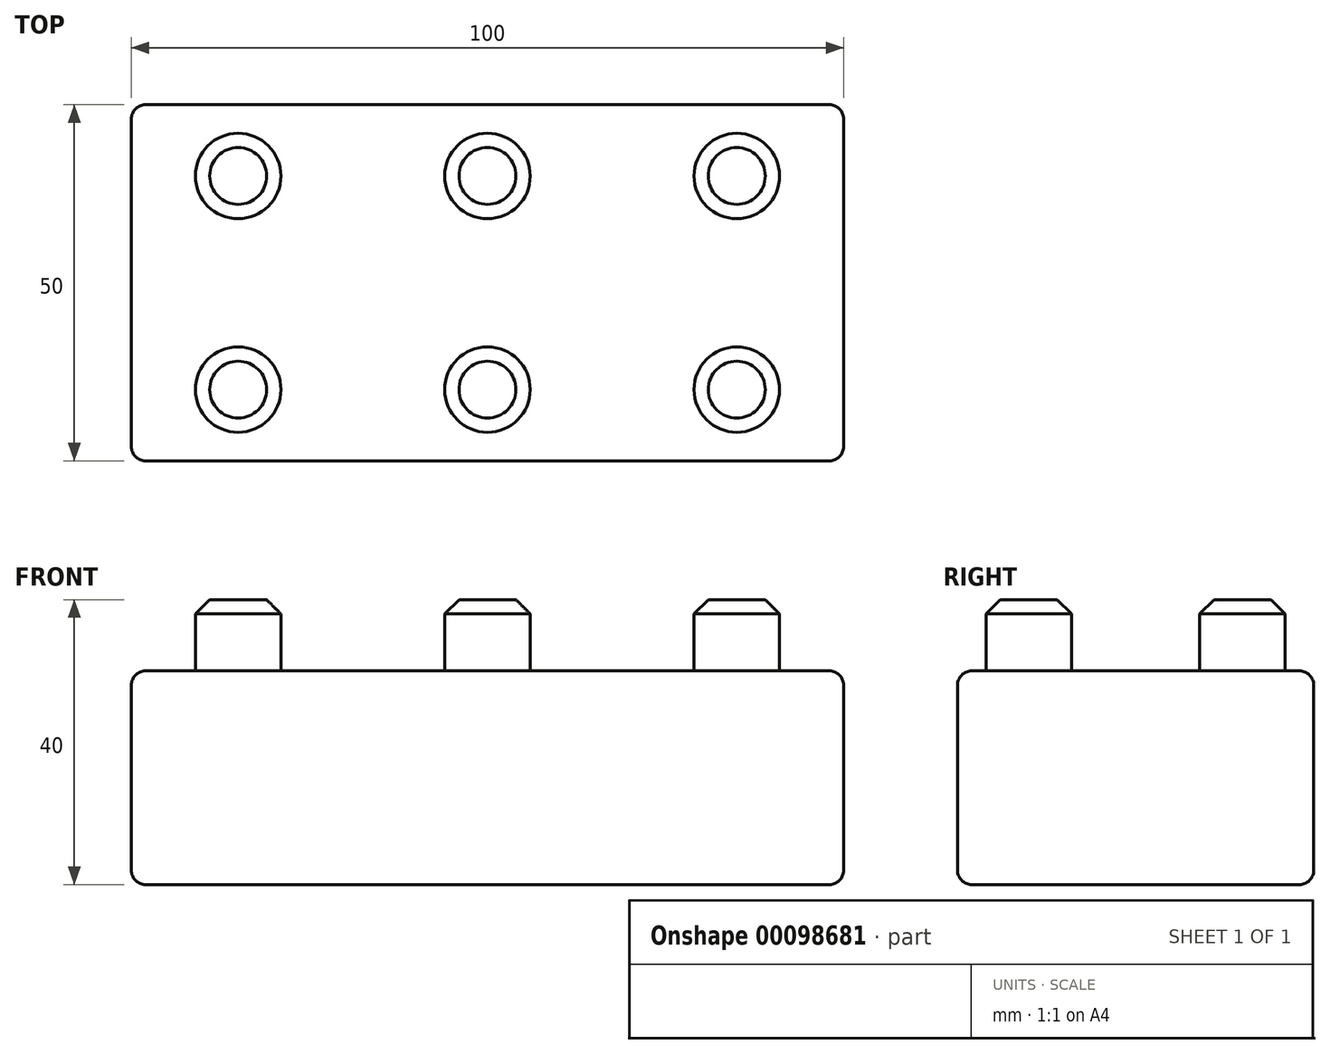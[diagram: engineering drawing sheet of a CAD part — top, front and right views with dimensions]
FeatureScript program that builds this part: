
annotation { "Feature Type Name" : "Feature", "Feature Type Description" : "" }
export const myFeature = defineFeature(function(context is Context, id is Id, definition is map)
    precondition{}
    {
        {
            var Q0;
            Q0=qCreatedBy(makeId("Top.planeOp"),FACE);
            var sketch = newSketch(context, id + "F0", { "sketchPlane" : qUnion([Q0])});
            skLineSegment(sketch, "E0.bottom", {"start": v(50, 25) * mm, "end": v(-50, 25) * mm});
            skLineSegment(sketch, "E0.top", {"start": v(50, -25) * mm, "end": v(-50, -25) * mm});
            skLineSegment(sketch, "E0.left", {"start": v(50, 25) * mm, "end": v(50, -25) * mm});
            skLineSegment(sketch, "E0.right", {"start": v(-50, 25) * mm, "end": v(-50, -25) * mm});
            skPoint(sketch, "E0.middle", {"position": v(0, 0) * mm});
            skSolve(sketch);
        }
        {
            var Q0;
            Q0=makeQuery(id+"F0.imprint","IMPRINT",FACE,{"disambiguationData":[TD([[makeQuery(id+"F0.imprint","IMPRINT",EDGE,{"derivedFrom":sQuery(id+"F0.wireOp",EDGE,"E0.bottom")}),1.0]])]});
            extrude(context, id + "F1", {"entities" : qUnion([Q0]), "depth" : 30 * mm});
        }
        {
            var Q0;
            Q0=makeQuery(id+"F1.opExtrude","CAP_FACE",FACE,{"disambiguationData":[OSD([sQuery(id+"F0.wireOp",EDGE,"E0.bottom"),sQuery(id+"F0.wireOp",EDGE,"E0.top"),sQuery(id+"F0.wireOp",EDGE,"E0.left"),sQuery(id+"F0.wireOp",EDGE,"E0.right")])],"isStart":false});
            var sketch = newSketch(context, id + "F2", { "sketchPlane" : qUnion([Q0])});
            skLineSegment(sketch, "E1", {"start": v(-50, 0) * mm, "end": v(-35, 0) * mm, "construction": true});
            skPoint(sketch, "E1.endSnap0", {"position": v(-50, 0) * mm});
            skLineSegment(sketch, "E2", {"start": v(-35, 0) * mm, "end": v(-35, 15) * mm, "construction": true});
            skCircle(sketch, "E3", {"center": v(-35, 15) * mm, "radius": 6 * mm});
            skCircle(sketch, "E4.0.1.0", {"center": v(-35, -15) * mm, "radius": 6 * mm});
            skCircle(sketch, "E4.1.0.0", {"center": v(0, 15) * mm, "radius": 6 * mm});
            skCircle(sketch, "E4.1.1.0", {"center": v(0, -15) * mm, "radius": 6 * mm});
            skCircle(sketch, "E4.2.0.0", {"center": v(35, 15) * mm, "radius": 6 * mm});
            skCircle(sketch, "E4.2.1.0", {"center": v(35, -15) * mm, "radius": 6 * mm});
            skLineSegment(sketch, "E4.direction1", {"start": v(-35, 15) * mm, "end": v(0, 15) * mm, "construction": true});
            skLineSegment(sketch, "E4.direction2", {"start": v(-35, 15) * mm, "end": v(-35, -15) * mm, "construction": true});
            skSolve(sketch);
        }
        {
            var Q0;
            Q0=makeQuery(id+"F2.imprint","IMPRINT",FACE,{"disambiguationData":[TD([[makeQuery(id+"F2.imprint","IMPRINT",EDGE,{"derivedFrom":sQuery(id+"F2.wireOp",EDGE,"E4.2.0.0")}),1.0]])]});
            var Q1;
            Q1=makeQuery(id+"F2.imprint","IMPRINT",FACE,{"disambiguationData":[TD([[makeQuery(id+"F2.imprint","IMPRINT",EDGE,{"derivedFrom":sQuery(id+"F2.wireOp",EDGE,"E4.2.1.0")}),1.0]])]});
            var Q2;
            Q2=makeQuery(id+"F2.imprint","IMPRINT",FACE,{"disambiguationData":[TD([[makeQuery(id+"F2.imprint","IMPRINT",EDGE,{"derivedFrom":sQuery(id+"F2.wireOp",EDGE,"E4.1.1.0")}),1.0]])]});
            var Q3;
            Q3=makeQuery(id+"F2.imprint","IMPRINT",FACE,{"disambiguationData":[TD([[makeQuery(id+"F2.imprint","IMPRINT",EDGE,{"derivedFrom":sQuery(id+"F2.wireOp",EDGE,"E4.1.0.0")}),1.0]])]});
            var Q4;
            Q4=makeQuery(id+"F2.imprint","IMPRINT",FACE,{"disambiguationData":[TD([[makeQuery(id+"F2.imprint","IMPRINT",EDGE,{"derivedFrom":sQuery(id+"F2.wireOp",EDGE,"E3")}),1.0]])]});
            var Q5;
            Q5=makeQuery(id+"F2.imprint","IMPRINT",FACE,{"disambiguationData":[TD([[makeQuery(id+"F2.imprint","IMPRINT",EDGE,{"derivedFrom":sQuery(id+"F2.wireOp",EDGE,"E4.0.1.0")}),1.0]])]});
            extrude(context, id + "F3", {"entities" : qUnion([Q0, Q1, Q2, Q3, Q4, Q5]), "operationType" : NewBodyOperationType.ADD, "depth" : 10 * mm});
        }
        {
            var Q0;
            Q0=makeQuery(id+"F1.opExtrude","CAP_EDGE",EDGE,{"disambiguationData":[OSD([sQuery(id+"F0.wireOp",EDGE,"E0.left")])],"isStart":false});
            var Q1;
            Q1=makeQuery(id+"F1.opExtrude","CAP_EDGE",EDGE,{"disambiguationData":[OSD([sQuery(id+"F0.wireOp",EDGE,"E0.top")])],"isStart":false});
            var Q2;
            Q2=makeQuery(id+"F1.opExtrude","CAP_EDGE",EDGE,{"disambiguationData":[OSD([sQuery(id+"F0.wireOp",EDGE,"E0.bottom")])],"isStart":false});
            var Q3;
            Q3=makeQuery(id+"F1.opExtrude","CAP_EDGE",EDGE,{"disambiguationData":[OSD([sQuery(id+"F0.wireOp",EDGE,"E0.right")])],"isStart":false});
            var Q4;
            Q4=makeQuery(id+"F1.opExtrude","SWEPT_FACE",FACE,{"disambiguationData":[OSD([sQuery(id+"F0.wireOp",EDGE,"E0.left")])]});
            var Q5;
            Q5=makeQuery(id+"F1.opExtrude","SWEPT_FACE",FACE,{"disambiguationData":[OSD([sQuery(id+"F0.wireOp",EDGE,"E0.top")])]});
            var Q6;
            Q6=makeQuery(id+"F1.opExtrude","SWEPT_FACE",FACE,{"disambiguationData":[OSD([sQuery(id+"F0.wireOp",EDGE,"E0.bottom")])]});
            var Q7;
            Q7=makeQuery(id+"F1.opExtrude","SWEPT_FACE",FACE,{"disambiguationData":[OSD([sQuery(id+"F0.wireOp",EDGE,"E0.right")])]});
            fillet(context, id + "F4", {"entities" : qUnion([Q0, Q1, Q2, Q3, Q4, Q5, Q6, Q7]), "radius" : 2 * mm, "tangentPropagation" : true, "allowEdgeOverflow" : false});
        }
        {
            var Q0;
            Q0=makeQuery(id+"F3.opExtrude","CAP_EDGE",EDGE,{"disambiguationData":[OSD([sQuery(id+"F2.wireOp",EDGE,"E3")])],"isStart":false});
            var Q1;
            Q1=makeQuery(id+"F3.opExtrude","CAP_EDGE",EDGE,{"disambiguationData":[OSD([sQuery(id+"F2.wireOp",EDGE,"E4.0.1.0")])],"isStart":false});
            var Q2;
            Q2=makeQuery(id+"F3.opExtrude","CAP_EDGE",EDGE,{"disambiguationData":[OSD([sQuery(id+"F2.wireOp",EDGE,"E4.1.1.0")])],"isStart":false});
            var Q3;
            Q3=makeQuery(id+"F3.opExtrude","CAP_EDGE",EDGE,{"disambiguationData":[OSD([sQuery(id+"F2.wireOp",EDGE,"E4.1.0.0")])],"isStart":false});
            var Q4;
            Q4=makeQuery(id+"F3.opExtrude","CAP_EDGE",EDGE,{"disambiguationData":[OSD([sQuery(id+"F2.wireOp",EDGE,"E4.2.0.0")])],"isStart":false});
            var Q5;
            Q5=makeQuery(id+"F3.opExtrude","CAP_EDGE",EDGE,{"disambiguationData":[OSD([sQuery(id+"F2.wireOp",EDGE,"E4.2.1.0")])],"isStart":false});
            chamfer(context, id + "F5", {"entities" : qUnion([Q0, Q1, Q2, Q3, Q4, Q5]), "width" : 2 * mm, "tangentPropagation" : true});
        }
        {
            var Q0;
            Q0=makeQuery(id+"F3.opExtrude","CAP_FACE",FACE,{"disambiguationData":[OSD([sQuery(id+"F2.wireOp",EDGE,"E4.0.1.0")])],"isStart":false});
            extrude(context, id + "F6", {"entities" : qUnion([Q0]), "operationType" : NewBodyOperationType.ADD, "oppositeDirection" : true, "depth" : 5 * mm});
        }
    });
